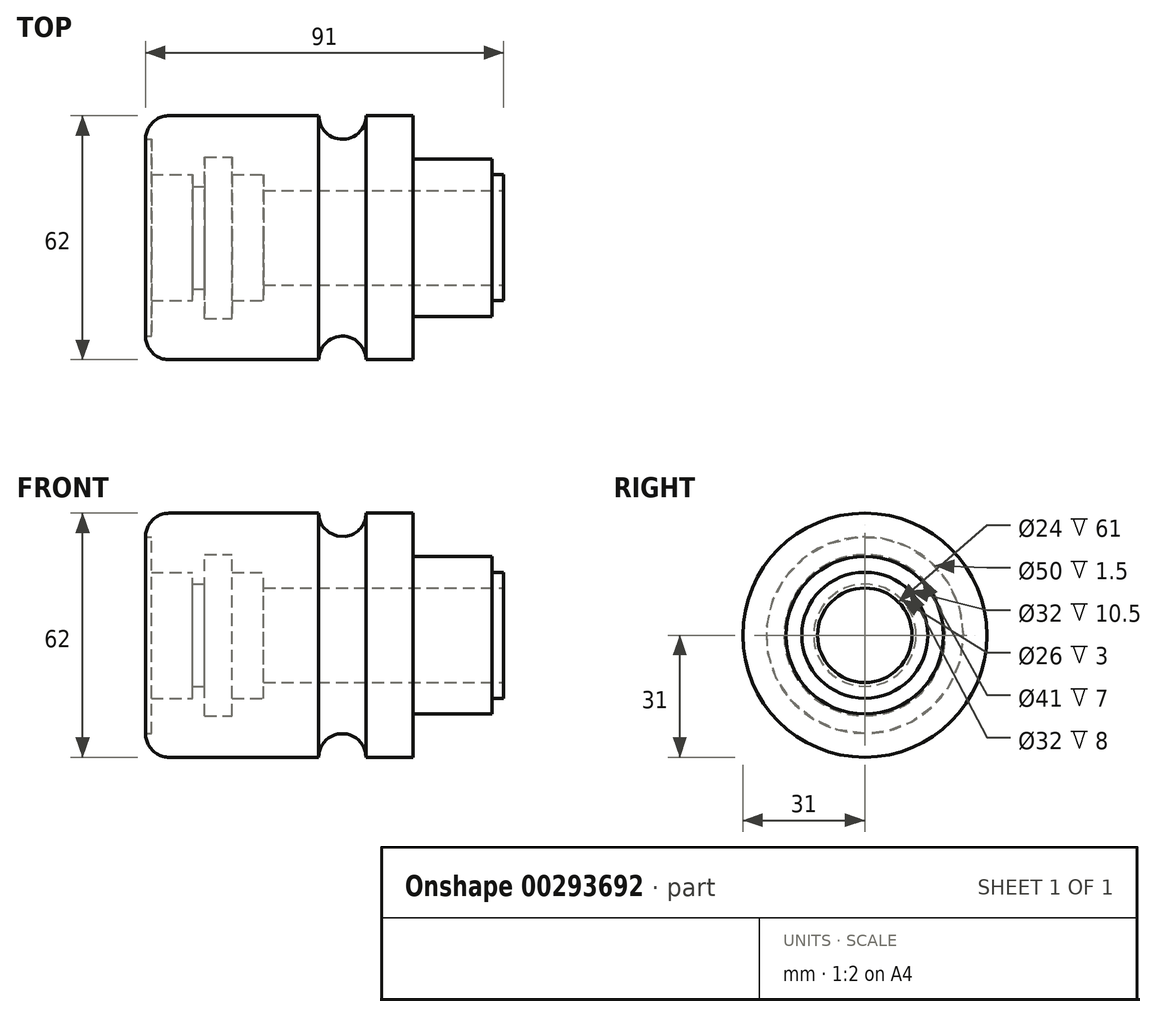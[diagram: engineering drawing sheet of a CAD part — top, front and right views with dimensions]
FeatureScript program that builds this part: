
annotation { "Feature Type Name" : "Feature", "Feature Type Description" : "" }
export const myFeature = defineFeature(function(context is Context, id is Id, definition is map)
    precondition{}
    {
        {
            var Q0;
            Q0=qCreatedBy(makeId("Front.planeOp"),FACE);
            var sketch = newSketch(context, id + "F0", { "sketchPlane" : qUnion([Q0])});
            skLineSegment(sketch, "E0", {"start": v(0, 0) * mm, "end": v(0, 25) * mm});
            skLineSegment(sketch, "E1", {"start": v(6, 31) * mm, "end": v(44, 31) * mm});
            skArc(sketch, "E2", {"start": v(44, 31) * mm, "mid": v(50, 25) * mm, "end": v(56, 31) * mm});
            skLineSegment(sketch, "E3", {"start": v(56, 31) * mm, "end": v(68, 31) * mm});
            skLineSegment(sketch, "E4", {"start": v(68, 31) * mm, "end": v(68, 20) * mm});
            skLineSegment(sketch, "E5", {"start": v(68, 20) * mm, "end": v(88, 20) * mm});
            skLineSegment(sketch, "E6", {"start": v(88, 20) * mm, "end": v(88, 16) * mm});
            skLineSegment(sketch, "E7", {"start": v(88, 16) * mm, "end": v(91, 16) * mm});
            skLineSegment(sketch, "E8", {"start": v(91, 16) * mm, "end": v(91, 0) * mm});
            skLineSegment(sketch, "E9", {"start": v(91, 0) * mm, "end": v(0, 0) * mm});
            skPoint(sketch, "E10.visualSharp", {"position": v(0, 31) * mm});
            skArc(sketch, "E10.filletArc", {"start": v(6, 31) * mm, "mid": v(1.76, 29.24) * mm, "end": v(0, 25) * mm});
            skLineSegment(sketch, "E11", {"start": v(12, 16) * mm, "end": v(12, 13) * mm});
            skLineSegment(sketch, "E12", {"start": v(12, 13) * mm, "end": v(15, 13) * mm});
            skLineSegment(sketch, "E13", {"start": v(15, 13) * mm, "end": v(15, 20.5) * mm});
            skLineSegment(sketch, "E14", {"start": v(15, 20.5) * mm, "end": v(22, 20.5) * mm});
            skLineSegment(sketch, "E15", {"start": v(22, 20.5) * mm, "end": v(22, 16) * mm});
            skLineSegment(sketch, "E16", {"start": v(22, 16) * mm, "end": v(30, 16) * mm});
            skLineSegment(sketch, "E17.0", {"start": v(1.5, 0) * mm, "end": v(1.5, 25) * mm});
            skLineSegment(sketch, "E18", {"start": v(12, 16) * mm, "end": v(1.5, 16) * mm});
            skLineSegment(sketch, "E19", {"start": v(30, 16) * mm, "end": v(30, 12) * mm});
            skLineSegment(sketch, "E20", {"start": v(30, 12) * mm, "end": v(91, 12) * mm});
            skLineSegment(sketch, "E21", {"start": v(0, 25) * mm, "end": v(1.5, 25) * mm});
            skSolve(sketch);
        }
        {
            var Q0;
            Q0=makeQuery(id+"F0.imprint","IMPRINT",FACE,{"disambiguationData":[TD([[makeQuery(id+"F0.imprint","IMPRINT",EDGE,{"derivedFrom":sQuery(id+"F0.wireOp",EDGE,"E1")}),-1.0]])]});
            var Q1;
            Q1=sQuery(id+"F0.wireOp",EDGE,"E9");
            revolve(context, id + "F1", {"entities" : qUnion([Q0]), "axis" : qUnion([Q1]), "revolveType" : RevolveType.FULL});
        }
    });
